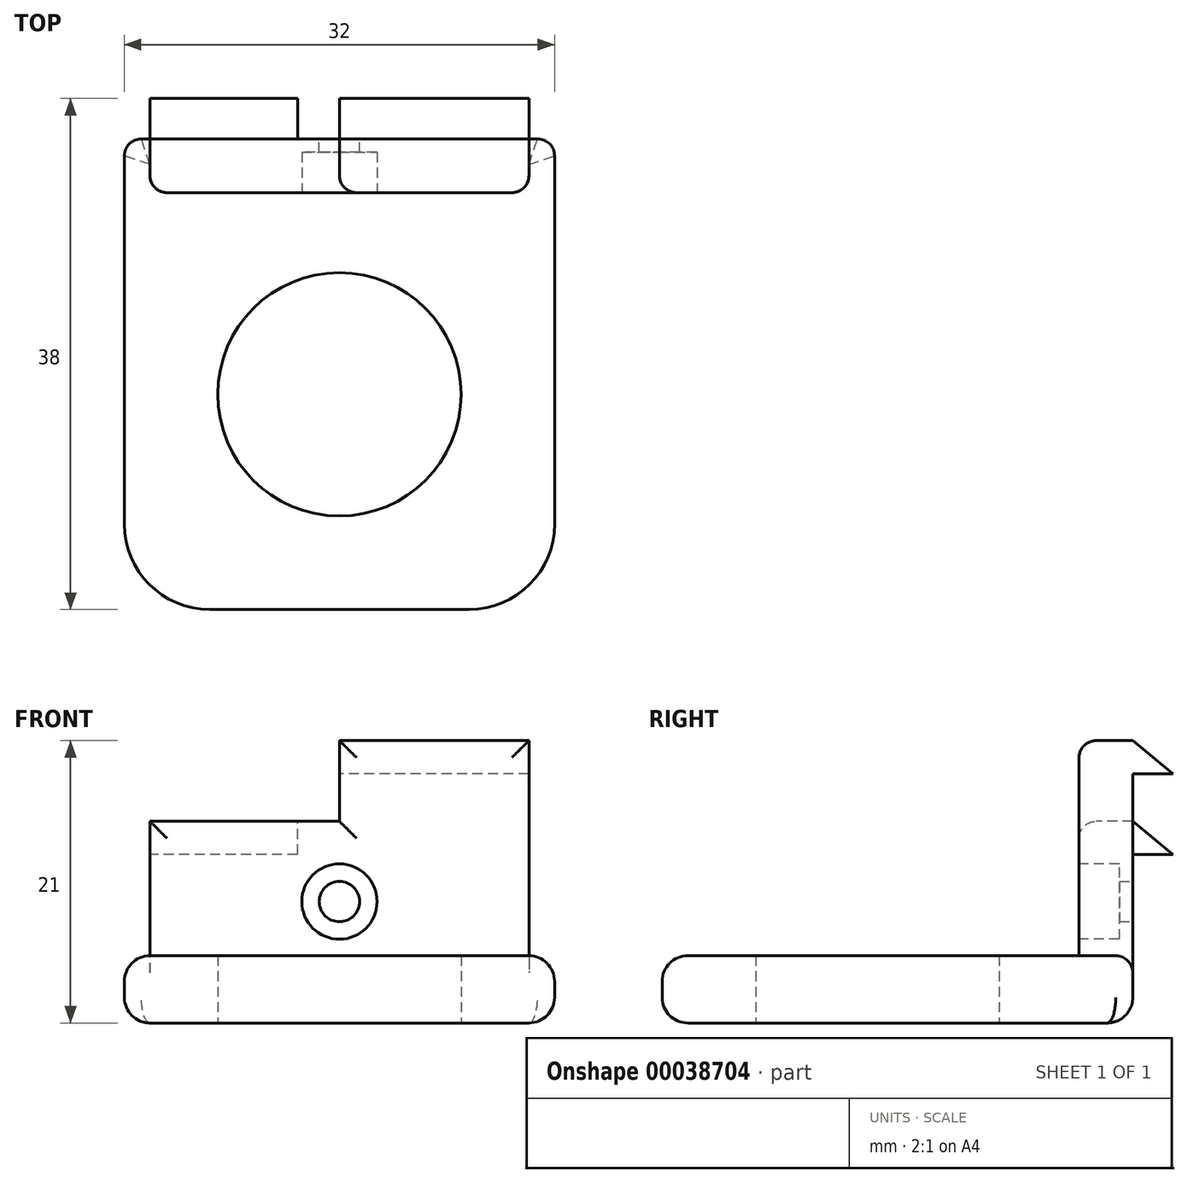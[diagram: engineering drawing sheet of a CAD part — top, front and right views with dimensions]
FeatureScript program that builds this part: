
annotation { "Feature Type Name" : "Feature", "Feature Type Description" : "" }
export const myFeature = defineFeature(function(context is Context, id is Id, definition is map)
    precondition{}
    {
        {
            var Q0;
            Q0=qCreatedBy(makeId("Top.planeOp"),FACE);
            var sketch = newSketch(context, id + "F0", { "sketchPlane" : qUnion([Q0])});
            skCircle(sketch, "E0", {"center": v(0, 0) * mm, "radius": 9.05 * mm});
            skLineSegment(sketch, "E1.bottom", {"start": v(-16, 19) * mm, "end": v(16, 19) * mm});
            skLineSegment(sketch, "E1.top", {"start": v(-9.65, -16) * mm, "end": v(9.65, -16) * mm});
            skLineSegment(sketch, "E1.left", {"start": v(-16, 19) * mm, "end": v(-16, -9.65) * mm});
            skLineSegment(sketch, "E1.right", {"start": v(16, 19) * mm, "end": v(16, -9.65) * mm});
            skPoint(sketch, "E2.visualSharp", {"position": v(-16, -16) * mm});
            skArc(sketch, "E2.filletArc", {"start": v(-16, -9.65) * mm, "mid": v(-14.14, -14.14) * mm, "end": v(-9.65, -16) * mm});
            skPoint(sketch, "E3.visualSharp", {"position": v(16, -16) * mm});
            skArc(sketch, "E3.filletArc", {"start": v(9.65, -16) * mm, "mid": v(14.14, -14.14) * mm, "end": v(16, -9.65) * mm});
            skSolve(sketch);
        }
        {
            var Q0;
            Q0=makeQuery(id+"F0.imprint","IMPRINT",FACE,{"disambiguationData":[TD([[makeQuery(id+"F0.imprint","IMPRINT",EDGE,{"derivedFrom":sQuery(id+"F0.wireOp",EDGE,"E0")}),-1.0]])]});
            extrude(context, id + "F1", {"entities" : qUnion([Q0]), "depth" : 5 * mm});
        }
        {
            var Q0;
            Q0=makeQuery(id+"F1.opExtrude","CAP_EDGE",EDGE,{"disambiguationData":[OSD([sQuery(id+"F0.wireOp",EDGE,"E1.bottom")])],"isStart":true});
            var Q1;
            Q1=makeQuery(id+"F1.opExtrude","CAP_EDGE",EDGE,{"disambiguationData":[OSD([sQuery(id+"F0.wireOp",EDGE,"E1.right")])],"isStart":true});
            fillet(context, id + "F2", {"entities" : qUnion([Q0, Q1]), "radius" : 1.9 * mm, "tangentPropagation" : true, "allowEdgeOverflow" : false});
        }
        {
            var Q0;
            Q0=makeQuery(id+"F1.opExtrude","CAP_EDGE",EDGE,{"disambiguationData":[OSD([sQuery(id+"F0.wireOp",EDGE,"E1.top")])],"isStart":false});
            var Q1;
            Q1=makeQuery(id+"F1.opExtrude","CAP_EDGE",EDGE,{"disambiguationData":[OSD([sQuery(id+"F0.wireOp",EDGE,"E1.right")])],"isStart":false});
            fillet(context, id + "F3", {"entities" : qUnion([Q0, Q1]), "radius" : 1.9 * mm, "tangentPropagation" : true, "allowEdgeOverflow" : false});
        }
        {
            var Q0;
            Q0=makeQuery(id+"F1.opExtrude","CAP_FACE",FACE,{"disambiguationData":[OSD([sQuery(id+"F0.wireOp",EDGE,"E0"),sQuery(id+"F0.wireOp",EDGE,"E1.bottom"),sQuery(id+"F0.wireOp",EDGE,"E1.top"),sQuery(id+"F0.wireOp",EDGE,"E1.left"),sQuery(id+"F0.wireOp",EDGE,"E1.right"),sQuery(id+"F0.wireOp",EDGE,"E2.filletArc"),sQuery(id+"F0.wireOp",EDGE,"E3.filletArc")])],"isStart":false});
            var sketch = newSketch(context, id + "F4", { "sketchPlane" : qUnion([Q0])});
            skLineSegment(sketch, "E4.bottom", {"start": v(-14.1, 19) * mm, "end": v(14.1, 19) * mm});
            skLineSegment(sketch, "E4.top", {"start": v(-14.1, 15) * mm, "end": v(14.1, 15) * mm});
            skLineSegment(sketch, "E4.left", {"start": v(-14.1, 19) * mm, "end": v(-14.1, 15) * mm});
            skLineSegment(sketch, "E4.right", {"start": v(14.1, 19) * mm, "end": v(14.1, 15) * mm});
            skSolve(sketch);
        }
        {
            var Q0;
            Q0=makeQuery(id+"F4.imprint","IMPRINT",FACE,{"disambiguationData":[TD([[makeQuery(id+"F4.imprint","IMPRINT",EDGE,{"derivedFrom":sQuery(id+"F4.wireOp",EDGE,"E4.bottom")}),-1.0]])]});
            extrude(context, id + "F5", {"entities" : qUnion([Q0]), "operationType" : NewBodyOperationType.ADD, "depth" : 10 * mm});
        }
        {
            var Q0;
            Q0=qCreatedBy(makeId("Right.planeOp"),FACE);
            var sketch = newSketch(context, id + "F6", { "sketchPlane" : qUnion([Q0])});
            skLineSegment(sketch, "E5", {"start": v(19, 15) * mm, "end": v(19, 12.53) * mm});
            skLineSegment(sketch, "E6", {"start": v(19, 12.53) * mm, "end": v(22, 12.53) * mm});
            skLineSegment(sketch, "E7", {"start": v(22, 12.53) * mm, "end": v(19, 15) * mm});
            skSolve(sketch);
        }
        {
            var Q0;
            Q0=makeQuery(id+"F6.imprint","IMPRINT",FACE,{"disambiguationData":[TD([[makeQuery(id+"F6.imprint","IMPRINT",EDGE,{"derivedFrom":sQuery(id+"F6.wireOp",EDGE,"E5")}),1.0]])]});
            var Q1;
            Q1=makeQuery(id+"F5.opExtrude","SWEPT_FACE",FACE,{"disambiguationData":[OSD([sQuery(id+"F4.wireOp",EDGE,"E4.right")])]});
            var Q2;
            Q2=makeQuery(id+"F5.opExtrude","SWEPT_FACE",FACE,{"disambiguationData":[OSD([sQuery(id+"F4.wireOp",EDGE,"E4.left")])]});
            extrude(context, id + "F7", {"entities" : qUnion([Q0]), "operationType" : NewBodyOperationType.ADD, "endBound" : BoundingType.UP_TO_SURFACE, "endBoundEntityFace" : qUnion([Q1]), "depth" : 25.4 * mm, "hasSecondDirection" : true, "secondDirectionBound" : SecondDirectionBoundingType.UP_TO_SURFACE, "secondDirectionOppositeDirection" : true, "secondDirectionBoundEntityFace" : qUnion([Q2]), "secondDirectionDepth" : 25.4 * mm});
        }
        {
            var Q0;
            Q0=makeQuery(id+"F5.boolean.opBoolean","MERGE",FACE,{"derivedFrom":[makeQuery(id+"F1.opExtrude","SWEPT_FACE",FACE,{"disambiguationData":[OSD([sQuery(id+"F0.wireOp",EDGE,"E1.bottom")])]}),makeQuery(id+"F5.opExtrude","SWEPT_FACE",FACE,{"disambiguationData":[OSD([sQuery(id+"F4.wireOp",EDGE,"E4.bottom")])]})]});
            var sketch = newSketch(context, id + "F8", { "sketchPlane" : qUnion([Q0])});
            skCircle(sketch, "E8", {"center": v(0, 9.03) * mm, "radius": 1.5 * mm});
            skSolve(sketch);
        }
        {
            var Q0;
            Q0=makeQuery(id+"F8.imprint","IMPRINT",FACE,{"disambiguationData":[TD([[makeQuery(id+"F8.imprint","IMPRINT",EDGE,{"derivedFrom":sQuery(id+"F8.wireOp",EDGE,"E8")}),1.0]])]});
            var Q1;
            Q1=makeQuery(id+"F5.opExtrude","SWEPT_FACE",FACE,{"disambiguationData":[OSD([sQuery(id+"F4.wireOp",EDGE,"E4.top")])]});
            extrude(context, id + "F9", {"entities" : qUnion([Q0]), "operationType" : NewBodyOperationType.REMOVE, "endBound" : BoundingType.UP_TO_SURFACE, "oppositeDirection" : true, "endBoundEntityFace" : qUnion([Q1]), "depth" : 25.4 * mm});
        }
        {
            var Q0;
            Q0=makeQuery(id+"F5.opExtrude","SWEPT_FACE",FACE,{"disambiguationData":[OSD([sQuery(id+"F4.wireOp",EDGE,"E4.top")])]});
            var sketch = newSketch(context, id + "F10", { "sketchPlane" : qUnion([Q0])});
            skCircle(sketch, "E9", {"center": v(0, 9.03) * mm, "radius": 2.8 * mm});
            skSolve(sketch);
        }
        {
            var Q0;
            Q0=makeQuery(id+"F10.imprint","IMPRINT",FACE,{"disambiguationData":[TD([[makeQuery(id+"F10.imprint","IMPRINT",EDGE,{"derivedFrom":sQuery(id+"F10.wireOp",EDGE,"E9")}),1.0]])]});
            extrude(context, id + "F11", {"entities" : qUnion([Q0]), "operationType" : NewBodyOperationType.REMOVE, "oppositeDirection" : true, "depth" : 3 * mm});
        }
        {
            var Q0;
            Q0=qCreatedBy(makeId("Right.planeOp"),FACE);
            var sketch = newSketch(context, id + "F12", { "sketchPlane" : qUnion([Q0])});
            skLineSegment(sketch, "E10", {"start": v(19, 11.1) * mm, "end": v(19, 15.11) * mm});
            skLineSegment(sketch, "E11", {"start": v(19, 15.11) * mm, "end": v(23.3, 12.23) * mm});
            skLineSegment(sketch, "E12", {"start": v(23.3, 12.23) * mm, "end": v(19, 11.1) * mm});
            skSolve(sketch);
        }
        {
            var Q0;
            Q0=makeQuery(id+"F12.imprint","IMPRINT",FACE,{"disambiguationData":[TD([[makeQuery(id+"F12.imprint","IMPRINT",EDGE,{"derivedFrom":sQuery(id+"F12.wireOp",EDGE,"E10")}),-1.0]])]});
            extrude(context, id + "F13", {"entities" : qUnion([Q0]), "operationType" : NewBodyOperationType.REMOVE, "depth" : 14.82 * mm, "hasSecondDirection" : true, "secondDirectionOppositeDirection" : true, "secondDirectionDepth" : 3.12 * mm});
        }
        {
            var Q0;
            Q0=makeQuery(id+"F5.opExtrude","CAP_FACE",FACE,{"disambiguationData":[OSD([sQuery(id+"F4.wireOp",EDGE,"E4.bottom"),sQuery(id+"F4.wireOp",EDGE,"E4.top"),sQuery(id+"F4.wireOp",EDGE,"E4.left"),sQuery(id+"F4.wireOp",EDGE,"E4.right")])],"isStart":false});
            var sketch = newSketch(context, id + "F14", { "sketchPlane" : qUnion([Q0])});
            skLineSegment(sketch, "E13.bottom", {"start": v(14.1, 15) * mm, "end": v(0, 15) * mm});
            skLineSegment(sketch, "E13.top", {"start": v(0, 19) * mm, "end": v(14.1, 19) * mm});
            skLineSegment(sketch, "E13.left", {"start": v(14.1, 19) * mm, "end": v(14.1, 15) * mm});
            skLineSegment(sketch, "E13.right", {"start": v(0, 19) * mm, "end": v(0, 15) * mm});
            skSolve(sketch);
        }
        {
            var Q0;
            Q0 = qSketchRegion(id + "F14", true);
            extrude(context, id + "F15", {"entities" : qUnion([Q0]), "operationType" : NewBodyOperationType.ADD, "depth" : 6 * mm});
        }
        {
            var Q0;
            Q0=qCreatedBy(makeId("Right.planeOp"),FACE);
            var sketch = newSketch(context, id + "F16", { "sketchPlane" : qUnion([Q0])});
            skLineSegment(sketch, "E14", {"start": v(19, 21) * mm, "end": v(22, 18.53) * mm});
            skLineSegment(sketch, "E15", {"start": v(22, 18.53) * mm, "end": v(19, 18.53) * mm});
            skLineSegment(sketch, "E16", {"start": v(19, 18.53) * mm, "end": v(19, 21) * mm});
            skSolve(sketch);
        }
        {
            var Q0;
            Q0=makeQuery(id+"F16.imprint","IMPRINT",FACE,{"disambiguationData":[TD([[makeQuery(id+"F16.imprint","IMPRINT",EDGE,{"derivedFrom":sQuery(id+"F16.wireOp",EDGE,"E14")}),-1.0]])]});
            var Q1;
            Q1=makeQuery(id+"F15.opExtrude","SWEPT_FACE",FACE,{"disambiguationData":[OSD([sQuery(id+"F14.wireOp",EDGE,"E13.left")])]});
            extrude(context, id + "F17", {"entities" : qUnion([Q0]), "operationType" : NewBodyOperationType.ADD, "endBound" : BoundingType.UP_TO_SURFACE, "endBoundEntityFace" : qUnion([Q1]), "depth" : 25.4 * mm});
        }
        {
            var Q0;
            Q0=makeQuery(id+"F5.opExtrude","SWEPT_EDGE",EDGE,{"disambiguationData":[OSD([sQuery(id+"F0.wireOp",EDGE,"E0"),sQuery(id+"F0.wireOp",EDGE,"E1.bottom"),sQuery(id+"F0.wireOp",EDGE,"E1.top"),sQuery(id+"F0.wireOp",EDGE,"E1.left"),sQuery(id+"F0.wireOp",EDGE,"E1.right"),sQuery(id+"F0.wireOp",EDGE,"E2.filletArc"),sQuery(id+"F0.wireOp",EDGE,"E3.filletArc"),sQuery(id+"F4.wireOp",EDGE,"E4.top"),sQuery(id+"F4.wireOp",EDGE,"E4.right")])]});
            var Q1;
            Q1=makeQuery(id+"F15.boolean.opBoolean","MERGE",EDGE,{"derivedFrom":[makeQuery(id+"F5.opExtrude","SWEPT_EDGE",EDGE,{"disambiguationData":[OSD([sQuery(id+"F0.wireOp",EDGE,"E0"),sQuery(id+"F0.wireOp",EDGE,"E1.bottom"),sQuery(id+"F0.wireOp",EDGE,"E1.top"),sQuery(id+"F0.wireOp",EDGE,"E1.left"),sQuery(id+"F0.wireOp",EDGE,"E1.right"),sQuery(id+"F0.wireOp",EDGE,"E2.filletArc"),sQuery(id+"F0.wireOp",EDGE,"E3.filletArc"),sQuery(id+"F4.wireOp",EDGE,"E4.top"),sQuery(id+"F4.wireOp",EDGE,"E4.left")])]}),makeQuery(id+"F15.opExtrude","SWEPT_EDGE",EDGE,{"disambiguationData":[OSD([sQuery(id+"F14.wireOp",EDGE,"E13.bottom"),sQuery(id+"F14.wireOp",EDGE,"E13.right")])]})]});
            var Q2;
            Q2=makeQuery(id+"F15.opExtrude","CAP_EDGE",EDGE,{"disambiguationData":[OSD([sQuery(id+"F14.wireOp",EDGE,"E13.bottom")])],"isStart":false});
            var Q3;
            Q3=makeQuery(id+"F5.opExtrude","CAP_EDGE",EDGE,{"disambiguationData":[OSD([sQuery(id+"F4.wireOp",EDGE,"E4.top")])],"isStart":false});
            var Q4;
            Q4=makeQuery(id+"F15.opExtrude","SWEPT_EDGE",EDGE,{"disambiguationData":[OSD([sQuery(id+"F4.wireOp",EDGE,"E4.top"),sQuery(id+"F14.wireOp",EDGE,"E13.bottom"),sQuery(id+"F14.wireOp",EDGE,"E13.right")])]});
            var Q5;
            Q5=makeQuery(id+"F5.opExtrude","SWEPT_EDGE",EDGE,{"disambiguationData":[OSD([sQuery(id+"F0.wireOp",EDGE,"E0"),sQuery(id+"F0.wireOp",EDGE,"E1.bottom"),sQuery(id+"F0.wireOp",EDGE,"E1.top"),sQuery(id+"F0.wireOp",EDGE,"E1.left"),sQuery(id+"F0.wireOp",EDGE,"E1.right"),sQuery(id+"F0.wireOp",EDGE,"E2.filletArc"),sQuery(id+"F0.wireOp",EDGE,"E3.filletArc"),sQuery(id+"F4.wireOp",EDGE,"E4.top"),sQuery(id+"F4.wireOp",EDGE,"E4.left")])]});
            fillet(context, id + "F18", {"entities" : qUnion([Q0, Q1, Q2, Q3, Q4, Q5]), "radius" : 1.27 * mm, "tangentPropagation" : true, "allowEdgeOverflow" : false});
        }
        {
            var Q0;
            Q0=makeQuery(id+"F1.opExtrude","SWEPT_EDGE",EDGE,{"disambiguationData":[OSD([sQuery(id+"F0.wireOp",EDGE,"E1.bottom"),sQuery(id+"F0.wireOp",EDGE,"E1.left")])]});
            var Q1;
            Q1=makeQuery(id+"F1.opExtrude","SWEPT_EDGE",EDGE,{"disambiguationData":[OSD([sQuery(id+"F0.wireOp",EDGE,"E1.bottom"),sQuery(id+"F0.wireOp",EDGE,"E1.right")])]});
            fillet(context, id + "F19", {"entities" : qUnion([Q0, Q1]), "radius" : 1.27 * mm, "tangentPropagation" : true, "allowEdgeOverflow" : false});
        }
    });
